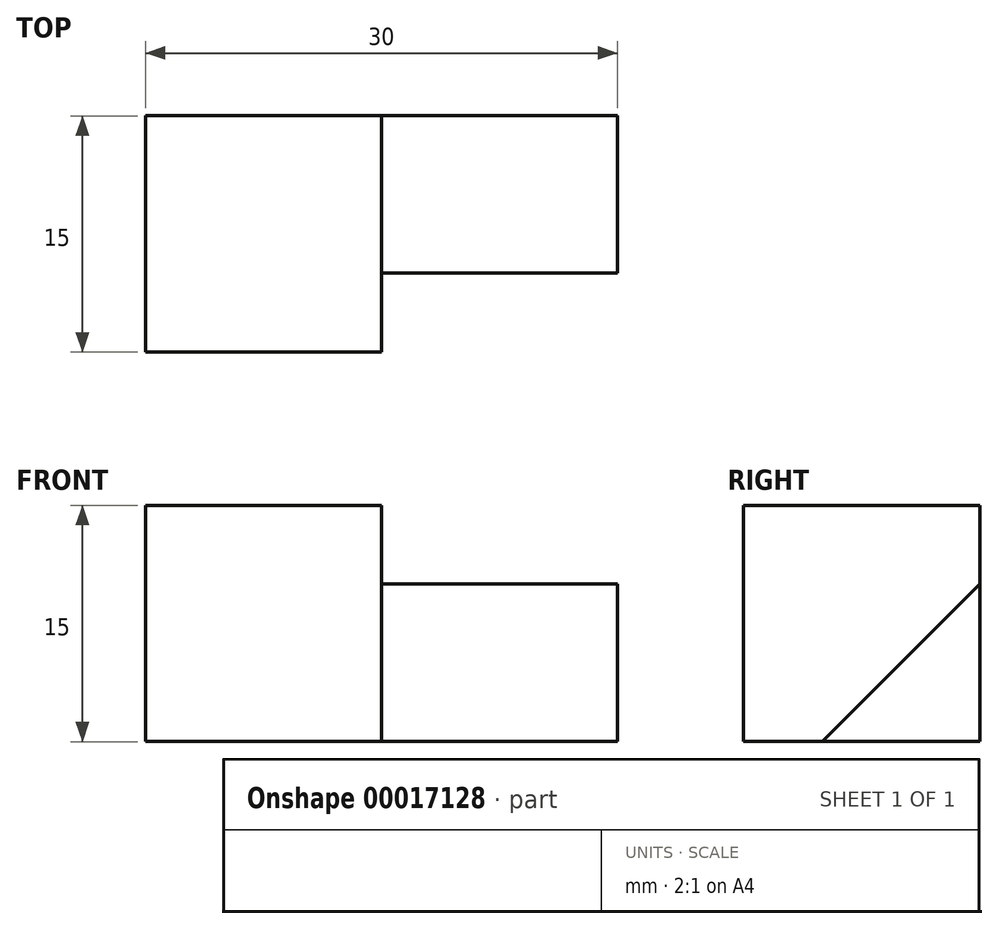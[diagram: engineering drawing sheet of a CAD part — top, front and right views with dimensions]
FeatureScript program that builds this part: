
annotation { "Feature Type Name" : "Feature", "Feature Type Description" : "" }
export const myFeature = defineFeature(function(context is Context, id is Id, definition is map)
    precondition{}
    {
        {
            var Q0;
            Q0=qCreatedBy(makeId("Right.planeOp"),FACE);
            var sketch = newSketch(context, id + "F0", { "sketchPlane" : qUnion([Q0])});
            skLineSegment(sketch, "E0.bottom", {"start": v(-2.14, 10.86) * mm, "end": v(12.86, 10.86) * mm});
            skLineSegment(sketch, "E0.top", {"start": v(-2.14, -4.14) * mm, "end": v(12.86, -4.14) * mm});
            skLineSegment(sketch, "E0.left", {"start": v(-2.14, 10.86) * mm, "end": v(-2.14, -4.14) * mm});
            skLineSegment(sketch, "E0.right", {"start": v(12.86, 10.86) * mm, "end": v(12.86, -4.14) * mm});
            skSolve(sketch);
        }
        {
            var Q0;
            Q0 = qSketchRegion(id + "F0", true);
            extrude(context, id + "F1", {"entities" : qUnion([Q0]), "depth" : 15 * mm});
        }
        {
            var Q0;
            Q0=makeQuery(id+"F1.opExtrude","CAP_FACE",FACE,{"disambiguationData":[OSD([sQuery(id+"F0.wireOp",EDGE,"E0.bottom"),sQuery(id+"F0.wireOp",EDGE,"E0.top"),sQuery(id+"F0.wireOp",EDGE,"E0.left"),sQuery(id+"F0.wireOp",EDGE,"E0.right")])],"isStart":false});
            var sketch = newSketch(context, id + "F2", { "sketchPlane" : qUnion([Q0])});
            skLineSegment(sketch, "E1", {"start": v(12.86, -4.14) * mm, "end": v(12.86, 5.86) * mm});
            skLineSegment(sketch, "E2", {"start": v(2.86, -4.14) * mm, "end": v(12.86, -4.14) * mm});
            skLineSegment(sketch, "E3", {"start": v(2.86, -4.14) * mm, "end": v(12.86, 5.86) * mm});
            skSolve(sketch);
        }
        {
            var Q0;
            Q0 = qSketchRegion(id + "F2", true);
            extrude(context, id + "F3", {"entities" : qUnion([Q0]), "operationType" : NewBodyOperationType.ADD, "depth" : 15 * mm});
        }
    });
